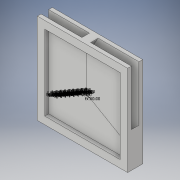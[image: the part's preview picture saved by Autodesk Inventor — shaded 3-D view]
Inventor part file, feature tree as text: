
AUTODESK INVENTOR PART (.ipt)
format: ipt  version: 2017 (Build 210142000, 142)  size: 305,152 bytes
history: native  units: in
note: dims shown in document units (in); Inventor stores cm internally (conversion verified against a paired STEP export)
features: extrude x6, sketch x5, other x4, plane x1
ambient origin geometry x8: Origin, YZ Plane, XZ Plane, XY Plane, X Axis, Y Axis, Z Axis, Center Point
bodies: Body1 (feature_tree), Body2 (feature_tree), Body3 (feature_tree), Body4 (feature_tree)
feature tree (16):
  other  "rame of door"
  extrude  "frame"  Depth=100.0in
  plane  "Work Plane3"
  extrude  "door slot bottom"  Depth=10.0in
  sketch  "Sketch5"  dims[d3=10.0in d4=10.0in]
  extrude  "doors sketch"  Depth=10.0in
  extrude  "top left door"  Depth=10.0in TaperAngle=0.0deg
  extrude  "top right door"  TaperAngle=60.0deg  [1 undecoded]
  extrude  "top left and right slots"  TaperAngle=60.0deg  [1 undecoded]
  sketch  "Sketch6"  dims[d5=10.0in d6=10.0in]
  sketch  "Sketch1"  dims[d0=100.0in d1=100.0in]
  other  "bottom of door"
  sketch  "Sketch7"  dims[d7=20.0in d8=0.0in d21=10.0in d22=0.0in]
  sketch  "Sketch8"  dims[d118=0.7071in d178=0.8316in d247=60.0deg d248=60.0deg d326=1.0in d327=1.0in d328=1.5in d329=1.5in d330=1.5in d331=1.0in d332=1.5in d390=1.0in d391=1.0in d392=1.0in d393=1.5in d394=1.5in d395=1.5in d396=1.0in d397=1.5in d398=1.0in d399=1.0in d400=1.0in d401=1.5in d402=1.5in d403=1.5in d404=1.0in d405=1.5in d406=1.0in d407=1.0in d408=1.0in d409=1.5in d410=1.5in d411=1.5in d412=1.0in d413=1.5in d414=1.0in d415=1.0in d416=1.0in d417=1.5in d418=1.5in d419=1.5in d420=1.0in d421=1.5in d422=1.0in d423=1.0in d424=1.0in d425=1.5in d426=1.5in d427=1.5in d428=1.0in d429=1.5in d430=1.0in d431=1.0in d432=1.0in d433=1.5in d434=1.5in d435=1.5in d436=1.0in d437=1.5in d438=1.0in d439=1.0in d440=1.0in d441=1.5in d442=1.5in d443=1.5in d444=1.0in d445=1.5in d446=1.0in d447=1.0in d448=1.0in d449=1.5in d450=1.5in d459=10.0in d460=0.0in d865=10.0in d866=0.0in d867=10.0in d868=0.0in d869=10.0in d870=0.0in]
  other  "top right of door"
  other  "top left of door"
note: 2 required parameter values undecoded (feature->parameter linkage not recoverable at this tier; creation-order binding heuristic only, values carry confidence <= 0.55)
